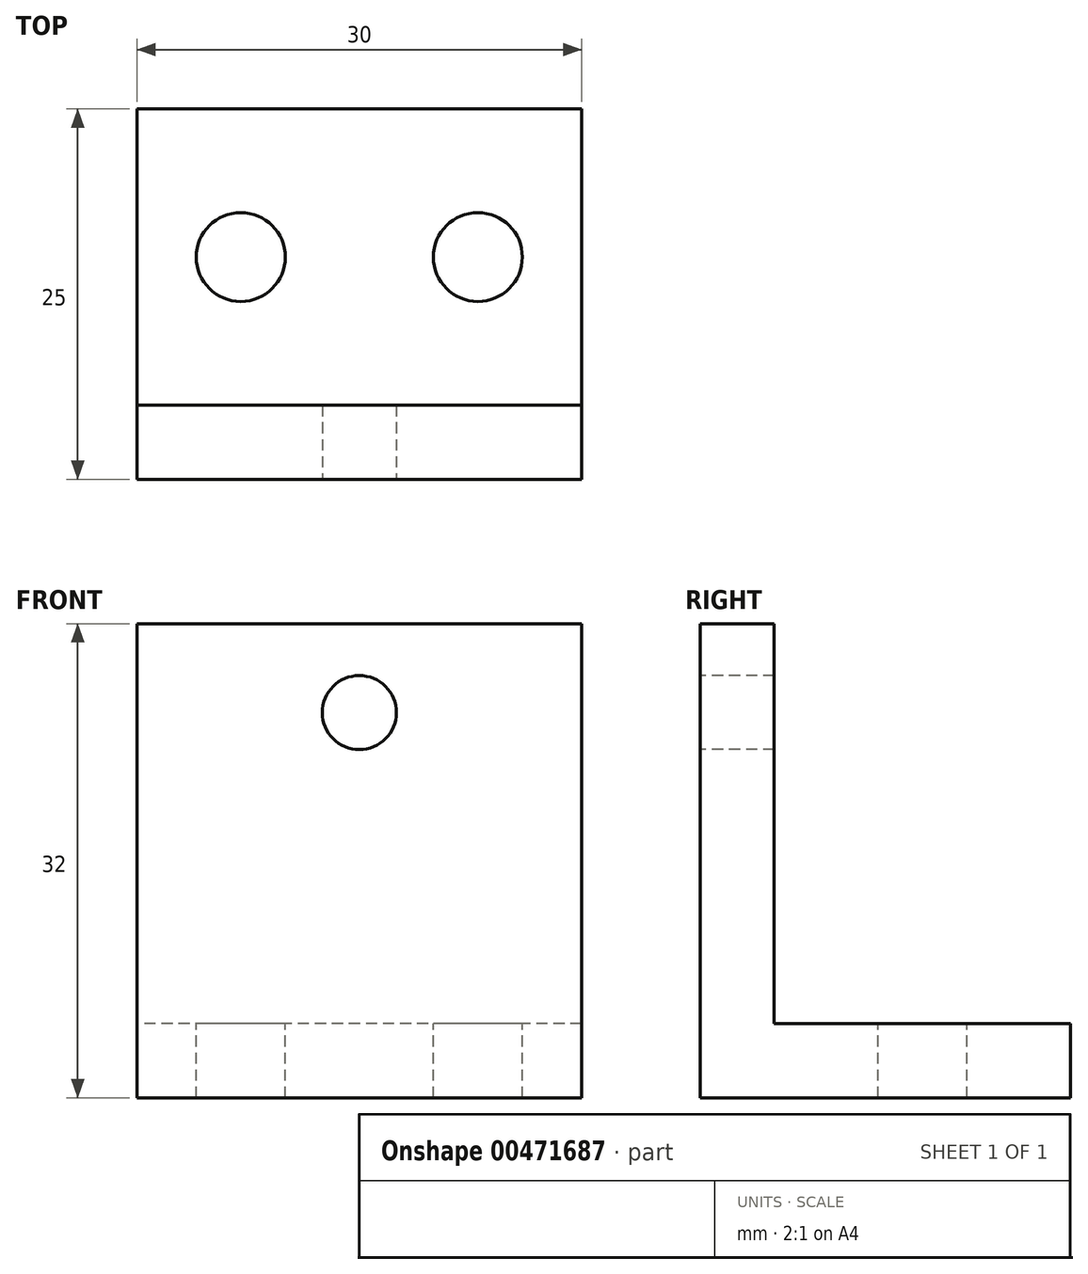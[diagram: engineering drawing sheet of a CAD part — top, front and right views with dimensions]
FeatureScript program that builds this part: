
annotation { "Feature Type Name" : "Feature", "Feature Type Description" : "" }
export const myFeature = defineFeature(function(context is Context, id is Id, definition is map)
    precondition{}
    {
        {
            var Q0;
            Q0=qCreatedBy(makeId("Front.planeOp"),FACE);
            var sketch = newSketch(context, id + "F0", { "sketchPlane" : qUnion([Q0])});
            skLineSegment(sketch, "E0.bottom", {"start": v(0, 0) * mm, "end": v(30, 0) * mm});
            skLineSegment(sketch, "E0.top", {"start": v(0, 32) * mm, "end": v(30, 32) * mm});
            skLineSegment(sketch, "E0.left", {"start": v(0, 0) * mm, "end": v(0, 32) * mm});
            skLineSegment(sketch, "E0.right", {"start": v(30, 0) * mm, "end": v(30, 32) * mm});
            skSolve(sketch);
        }
        {
            var Q0;
            Q0 = qSketchRegion(id + "F0", true);
            extrude(context, id + "F1", {"entities" : qUnion([Q0]), "depth" : 5 * mm});
        }
        {
            var Q0;
            Q0=makeQuery(id+"F1.opExtrude","CAP_FACE",FACE,{"disambiguationData":[OSD([sQuery(id+"F0.wireOp",EDGE,"E0.bottom"),sQuery(id+"F0.wireOp",EDGE,"E0.top"),sQuery(id+"F0.wireOp",EDGE,"E0.left"),sQuery(id+"F0.wireOp",EDGE,"E0.right")])],"isStart":true});
            var sketch = newSketch(context, id + "F2", { "sketchPlane" : qUnion([Q0])});
            skLineSegment(sketch, "E1.bottom", {"start": v(-30, 0) * mm, "end": v(0, 0) * mm});
            skLineSegment(sketch, "E1.top", {"start": v(-30, 5) * mm, "end": v(0, 5) * mm});
            skLineSegment(sketch, "E1.left", {"start": v(-30, 0) * mm, "end": v(-30, 5) * mm});
            skLineSegment(sketch, "E1.right", {"start": v(0, 0) * mm, "end": v(0, 5) * mm});
            skSolve(sketch);
        }
        {
            var Q0;
            Q0 = qSketchRegion(id + "F2", true);
            extrude(context, id + "F3", {"entities" : qUnion([Q0]), "operationType" : NewBodyOperationType.ADD, "depth" : 20 * mm});
        }
        {
            var Q0;
            Q0=makeQuery(id+"F3.opExtrude","SWEPT_FACE",FACE,{"disambiguationData":[OSD([sQuery(id+"F2.wireOp",EDGE,"E1.top")])]});
            var sketch = newSketch(context, id + "F4", { "sketchPlane" : qUnion([Q0])});
            skCircle(sketch, "E2", {"center": v(23, 10) * mm, "radius": 3 * mm});
            skPoint(sketch, "E2.centerSnap0", {"position": v(30, 10) * mm});
            skCircle(sketch, "E3", {"center": v(7, 10) * mm, "radius": 3 * mm});
            skPoint(sketch, "E3.centerSnap0", {"position": v(0, 10) * mm});
            skSolve(sketch);
        }
        {
            var Q0;
            Q0 = qSketchRegion(id + "F4", true);
            extrude(context, id + "F5", {"entities" : qUnion([Q0]), "operationType" : NewBodyOperationType.REMOVE, "oppositeDirection" : true, "depth" : 25 * mm});
        }
        {
            var Q0;
            Q0=makeQuery(id+"F1.opExtrude","CAP_FACE",FACE,{"disambiguationData":[OSD([sQuery(id+"F0.wireOp",EDGE,"E0.bottom"),sQuery(id+"F0.wireOp",EDGE,"E0.top"),sQuery(id+"F0.wireOp",EDGE,"E0.left"),sQuery(id+"F0.wireOp",EDGE,"E0.right")])],"isStart":false});
            var sketch = newSketch(context, id + "F6", { "sketchPlane" : qUnion([Q0])});
            skCircle(sketch, "E4", {"center": v(15, 26) * mm, "radius": 2.5 * mm});
            skPoint(sketch, "E4.centerSnap0", {"position": v(15, 32) * mm});
            skSolve(sketch);
        }
        {
            var Q0;
            Q0 = qSketchRegion(id + "F6", true);
            extrude(context, id + "F7", {"entities" : qUnion([Q0]), "operationType" : NewBodyOperationType.REMOVE, "oppositeDirection" : true, "depth" : 25 * mm});
        }
    });
